# Revit family: Турникет RTD-15
name_source: partatom
category: Generic Models
units: mm (PartAtom-declared; Revit-internal decimal feet)

## family parameters
Always vertical = Yes
Can host rebar = No
Cut with Voids When Loaded = No
Part Type = Normal
Room Calculation Point = No
Round Connector Dimension = Use Diameter
Shared = No
Work Plane-Based = No

## types (2) — shared parameters
Current = 5 A
Dimensions = 1600×1800×2325 mm
Electrical connection = 220 V
IP Code = IP54
Manufacturer = PERCo
Material = Housing and rotor ─ powder-coated aluminum
Number = 1
Operating temperature = from -40°C to +55°C
Passageway width = 755 mm
Rated power = 105 W
Rotor material = Steel painted RAL 1019
Throughput rate = 30 persons/min
Turnstile material = Steel painted RAL 1019
URL = https://www.perco.com
Unit of measurement = pcs
Voltage = 30 V
Weight = from 175 kg

## per-type parameters (varying)
| type | Full name | Name |
| RTD-15.1 motorized | RTD-15 Full-height rotary motorized turnstile | RTD-15 Rotary motorized turnstile |
| RTD-15.2 Electromechanical | RTD-15 Full-height rotary electromechanical turnstil | RTD-15 Electromechanical rotary turnstile |
